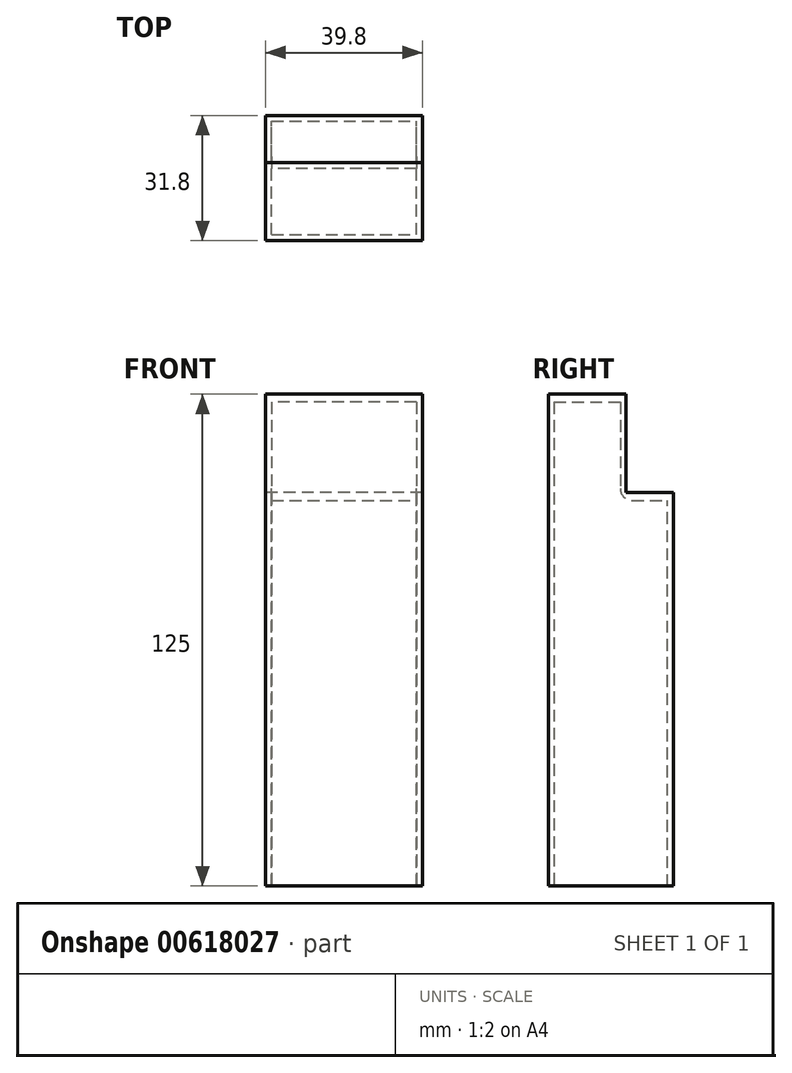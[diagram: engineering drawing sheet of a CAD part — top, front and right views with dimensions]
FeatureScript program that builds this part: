
annotation { "Feature Type Name" : "Feature", "Feature Type Description" : "" }
export const myFeature = defineFeature(function(context is Context, id is Id, definition is map)
    precondition{}
    {
        {
            var Q0;
            Q0=qCreatedBy(makeId("Top.planeOp"),FACE);
            var sketch = newSketch(context, id + "F0", { "sketchPlane" : qUnion([Q0])});
            skLineSegment(sketch, "E0.bottom", {"start": v(0, 0) * mm, "end": v(39.8, 0) * mm});
            skLineSegment(sketch, "E0.top", {"start": v(0, 31.8) * mm, "end": v(39.8, 31.8) * mm});
            skLineSegment(sketch, "E0.left", {"start": v(0, 0) * mm, "end": v(0, 31.8) * mm});
            skLineSegment(sketch, "E0.right", {"start": v(39.8, 0) * mm, "end": v(39.8, 31.8) * mm});
            skLineSegment(sketch, "E1.0", {"start": v(1.5, 30.3) * mm, "end": v(38.3, 30.3) * mm});
            skLineSegment(sketch, "E1.1", {"start": v(1.5, 1.5) * mm, "end": v(1.5, 30.3) * mm});
            skLineSegment(sketch, "E1.2", {"start": v(1.5, 1.5) * mm, "end": v(38.3, 1.5) * mm});
            skLineSegment(sketch, "E1.3", {"start": v(38.3, 1.5) * mm, "end": v(38.3, 30.3) * mm});
            skLineSegment(sketch, "E2", {"start": v(39.8, 19.8) * mm, "end": v(0, 19.8) * mm});
            skLineSegment(sketch, "E3", {"start": v(39.8, 18.3) * mm, "end": v(0, 18.3) * mm});
            skSolve(sketch);
        }
        {
            var Q0;
            {var subQ0=sQuery(id+"F0.wireOp",EDGE,"E3");var subQ1=sQuery(id+"F0.wireOp",EDGE,"E1.1");var subQ2=makeQuery(id+"F0.imprint","INTERSECT",VERTEX,{"derivedFrom":[subQ1,subQ0]});Q0=makeQuery(id+"F0.imprint","IMPRINT",FACE,{"disambiguationData":[TD([[makeQuery(id+"F0.imprint","IMPRINT",EDGE,{"disambiguationData":[TD([[subQ2,-1.0]])],"derivedFrom":subQ1}),-1.0]])]});}
            var Q1;
            {var subQ0=sQuery(id+"F0.wireOp",EDGE,"E2");var subQ1=sQuery(id+"F0.wireOp",EDGE,"E0.right");var subQ2=makeQuery(id+"F0.imprint","INTERSECT",VERTEX,{"derivedFrom":[subQ1,subQ0]});Q1=makeQuery(id+"F0.imprint","IMPRINT",FACE,{"disambiguationData":[TD([[makeQuery(id+"F0.imprint","IMPRINT",EDGE,{"disambiguationData":[TD([[subQ2,1.0]])],"derivedFrom":subQ1}),1.0]])]});}
            var Q2;
            {var subQ5=sQuery(id+"F0.wireOp",EDGE,"E0.bottom");Q2=makeQuery(id+"F0.imprint","IMPRINT",FACE,{"disambiguationData":[TD([[makeQuery(id+"F0.imprint","IMPRINT",EDGE,{"derivedFrom":subQ5}),1.0]])]});}
            var Q3;
            {var subQ0=sQuery(id+"F0.wireOp",EDGE,"E2");var subQ1=sQuery(id+"F0.wireOp",EDGE,"E0.left");var subQ2=makeQuery(id+"F0.imprint","INTERSECT",VERTEX,{"derivedFrom":[subQ1,subQ0]});Q3=makeQuery(id+"F0.imprint","IMPRINT",FACE,{"disambiguationData":[TD([[makeQuery(id+"F0.imprint","IMPRINT",EDGE,{"disambiguationData":[TD([[subQ2,1.0]])],"derivedFrom":subQ1}),-1.0]])]});}
            extrude(context, id + "F1", {"entities" : qUnion([Q0, Q1, Q2, Q3]), "depth" : 25 * mm, "offsetDistance" : 25 * mm});
        }
        {
            var Q0;
            {var subQ2=sQuery(id+"F0.wireOp",EDGE,"E0.top");Q0=makeQuery(id+"F0.imprint","IMPRINT",FACE,{"disambiguationData":[TD([[makeQuery(id+"F0.imprint","IMPRINT",EDGE,{"derivedFrom":subQ2}),-1.0]])]});}
            var Q1;
            {var subQ5=sQuery(id+"F0.wireOp",EDGE,"E0.bottom");Q1=makeQuery(id+"F0.imprint","IMPRINT",FACE,{"disambiguationData":[TD([[makeQuery(id+"F0.imprint","IMPRINT",EDGE,{"derivedFrom":subQ5}),1.0]])]});}
            var Q2;
            {var subQ0=sQuery(id+"F0.wireOp",EDGE,"E2");var subQ1=sQuery(id+"F0.wireOp",EDGE,"E0.right");var subQ2=makeQuery(id+"F0.imprint","INTERSECT",VERTEX,{"derivedFrom":[subQ1,subQ0]});Q2=makeQuery(id+"F0.imprint","IMPRINT",FACE,{"disambiguationData":[TD([[makeQuery(id+"F0.imprint","IMPRINT",EDGE,{"disambiguationData":[TD([[subQ2,1.0]])],"derivedFrom":subQ1}),1.0]])]});}
            var Q3;
            {var subQ0=sQuery(id+"F0.wireOp",EDGE,"E2");var subQ1=sQuery(id+"F0.wireOp",EDGE,"E0.left");var subQ2=makeQuery(id+"F0.imprint","INTERSECT",VERTEX,{"derivedFrom":[subQ1,subQ0]});Q3=makeQuery(id+"F0.imprint","IMPRINT",FACE,{"disambiguationData":[TD([[makeQuery(id+"F0.imprint","IMPRINT",EDGE,{"disambiguationData":[TD([[subQ2,1.0]])],"derivedFrom":subQ1}),-1.0]])]});}
            extrude(context, id + "F2", {"entities" : qUnion([Q0, Q1, Q2, Q3]), "operationType" : NewBodyOperationType.ADD, "oppositeDirection" : true, "depth" : 100 * mm, "offsetDistance" : 25 * mm});
        }
        {
            var Q0;
            {var subQ0=sQuery(id+"F0.wireOp",EDGE,"E1.0");Q0=makeQuery(id+"F0.imprint","IMPRINT",FACE,{"disambiguationData":[TD([[makeQuery(id+"F0.imprint","IMPRINT",EDGE,{"derivedFrom":subQ0}),-1.0]])]});}
            var Q1;
            {var subQ0=sQuery(id+"F0.wireOp",EDGE,"E3");var subQ1=sQuery(id+"F0.wireOp",EDGE,"E1.1");var subQ2=makeQuery(id+"F0.imprint","INTERSECT",VERTEX,{"derivedFrom":[subQ1,subQ0]});Q1=makeQuery(id+"F0.imprint","IMPRINT",FACE,{"disambiguationData":[TD([[makeQuery(id+"F0.imprint","IMPRINT",EDGE,{"disambiguationData":[TD([[subQ2,-1.0]])],"derivedFrom":subQ1}),-1.0]])]});}
            extrude(context, id + "F3", {"entities" : qUnion([Q0, Q1]), "operationType" : NewBodyOperationType.ADD, "oppositeDirection" : true, "depth" : 2 * mm, "offsetDistance" : 25 * mm});
        }
        {
            var Q0;
            Q0=makeQuery(id+"F3.opExtrude","CAP_EDGE",EDGE,{"disambiguationData":[OSD([sQuery(id+"F0.wireOp",EDGE,"E3")])],"isStart":false});
            fillet(context, id + "F4", {"entities" : qUnion([Q0]), "radius" : 3 * mm, "tangentPropagation" : true, "allowEdgeOverflow" : false});
        }
        {
            var Q0;
            Q0=makeQuery(id+"F1.opExtrude","CAP_FACE",FACE,{"disambiguationData":[OSD([sQuery(id+"F0.wireOp",EDGE,"E0.bottom"),sQuery(id+"F0.wireOp",EDGE,"E0.left"),sQuery(id+"F0.wireOp",EDGE,"E0.right"),sQuery(id+"F0.wireOp",EDGE,"E1.1"),sQuery(id+"F0.wireOp",EDGE,"E1.2"),sQuery(id+"F0.wireOp",EDGE,"E1.3"),sQuery(id+"F0.wireOp",EDGE,"E2"),sQuery(id+"F0.wireOp",EDGE,"E3")])],"isStart":false});
            var sketch = newSketch(context, id + "F5", { "sketchPlane" : qUnion([Q0])});
            skSolve(sketch);
        }
        {
            var Q0;
            Q0=makeQuery(id+"F5.imprint","IMPRINT",FACE,{"disambiguationData":[TD([[makeQuery(id+"F5.imprint","IMPRINT",EDGE,{"derivedFrom":makeQuery(id+"F1.opExtrude","CAP_EDGE",EDGE,{"disambiguationData":[OSD([sQuery(id+"F0.wireOp",EDGE,"E1.1")])],"isStart":false})}),-1.0]])]});
            extrude(context, id + "F6", {"entities" : qUnion([Q0]), "operationType" : NewBodyOperationType.ADD, "oppositeDirection" : true, "depth" : 2 * mm, "offsetDistance" : 25 * mm});
        }
    });
